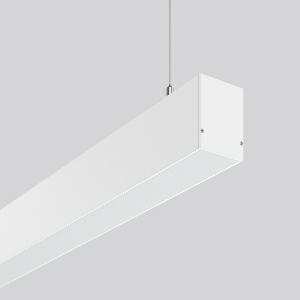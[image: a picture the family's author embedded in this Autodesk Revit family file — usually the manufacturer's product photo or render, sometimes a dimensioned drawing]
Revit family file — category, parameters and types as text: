
# Revit family: less_is_more_50_312312_002_1_76_3526
name_source: partatom
category: Lighting Fixtures
units: mm (PartAtom-declared; Revit-internal decimal feet)

## family parameters
Cut with Voids When Loaded = No
Host = Face
Light Source = No
Part Type = Normal
Room Calculation Point = No
Round Connector Dimension = Use Diameter
Shared = No

## types (1)
- LESS IS MORE 50 (1 x LED Modul 840, 3250 lm, 4000)
    Apparent Load = 28 VA
    CIE Flux Codes = 48 79 95 100 100
    Color Rendering = 80
    Color Temperature = 4000
    Default Elevation = 1800 mm
    Description = Series: LESS IS MORE 50
Linear pendant luminaire for aesthetically sophisticated lighting. Housing: extruded aluminium profile, powder-coated. End cap aluminium powder-coated. Canopy made of aluminium, powder-coated. Diffuser made of non-yellowing plastic (PMMA), opal. Direct light emission. Suitable for pendant. 2-point steel cable suspension freely positionable and infinitely height-adjustable. Special lengths available on request. LED unit with integrated converter interchangeable and removable. Suitable for through-wiring. With sensors or as a safety luminaire on request. 
Colour: traffic white, matt (RAL 9016)
Length: 1127 mm
Width: 57 mm
Height: 75 mm
Suspension length: 2000 mm
Lamp: LED
Socket: without socket
Colour temperature: 4000K
Colour rendering index (CRI): 80
System power: 28 W
Rated luminous flux: 3250 lm
Luminous efficiency: 116 lm/W
Control gear: Converter, dimmable, DALI
Protection class: I
Type of protection: IP 20
    Height = 75 mm
    Lamp = 1 x LED Modul 840
    Lamp Light Flux = 3250 lm
    Lamp count = 1
    Length = 1127 mm
    Lifetime = 50000 h
    Luminous efficacy = 116 lm/W
    Manufacturer = RZB
    ModVariant = No
    Model = 312312.002.1.76
    Mounting Place = Ceiling
    Mounting Type = Pendant
    Number of Poles = 1
    OnlyDefault = Yes
    Power Factor = 1
    Product Name = LESS IS MORE 50
    Product group = Pendant LED linear luminaires
    ProductGroupID = 907
    Protection Class = Protection class I
    Protection Degree = IP 20
    RLX_Detail_Level = 1
    RLX_Emergency_Light_Flux = 0 lm
    RLX_Emergency_Type = 0
    RLX_Emergency_Type_DB = No
    RlxData = <blob elided: 20641 chars, md5=b224c25a>
    Socket = socket
    Standby Power = 0 W
    System Light Flux = 3250 lm
    System Power = 28 W
    Type Comments = Product without accessories
    Type Image = 312318.002.jpg
    URL = http://relux.com
    VarID = ---
    Voltage = 230 V
    Voltage Range = 220-240 V
    Weight = 0.00 kg
    Width = 57 mm

## geometry (parser evidence)
native form markers: Blend x4, Sweep x11
no freeform markers — native parametric forms only
